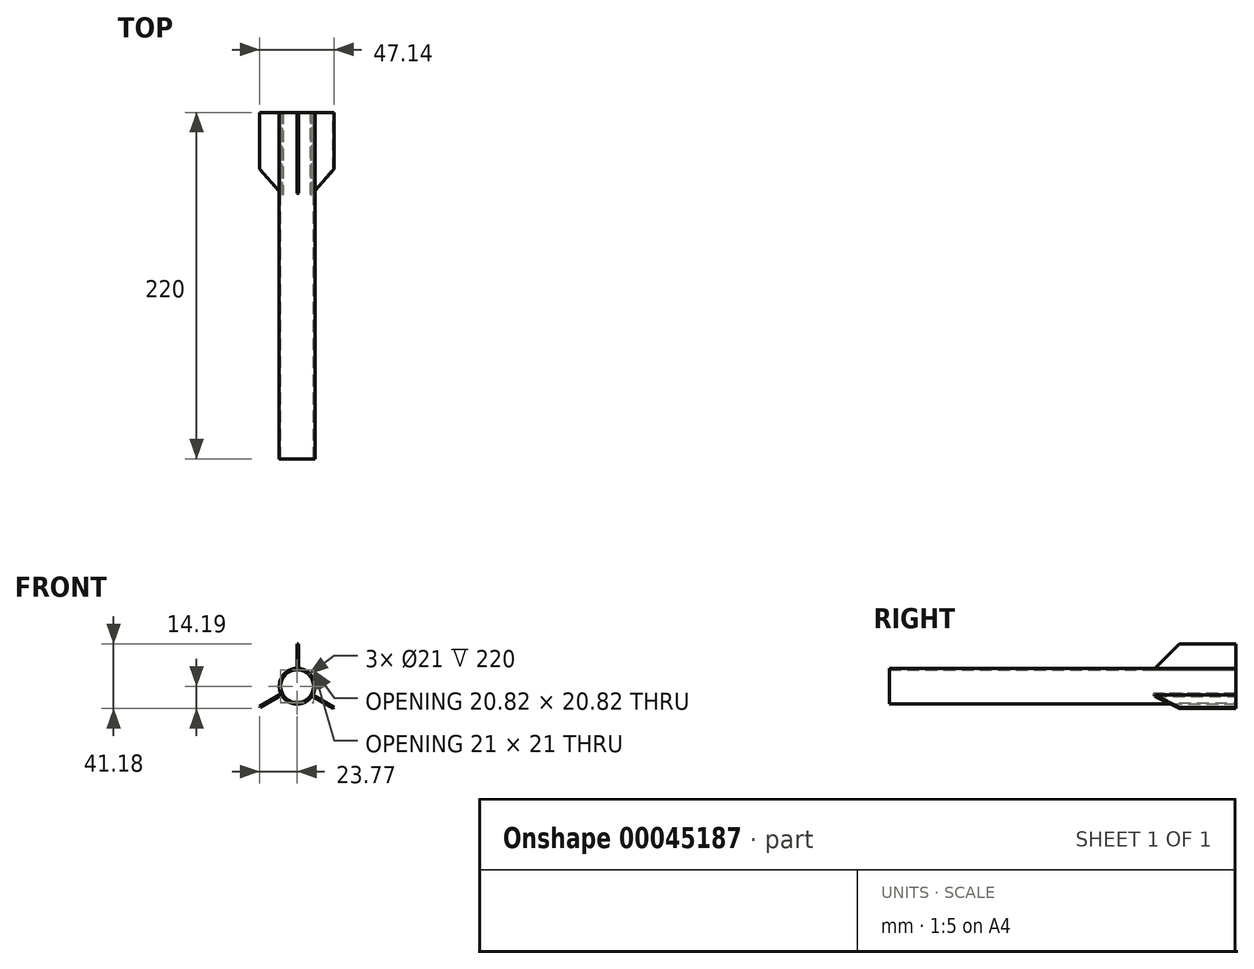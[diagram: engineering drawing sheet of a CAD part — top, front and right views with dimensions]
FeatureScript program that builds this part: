
annotation { "Feature Type Name" : "Feature", "Feature Type Description" : "" }
export const myFeature = defineFeature(function(context is Context, id is Id, definition is map)
    precondition{}
    {
        {
            var Q0;
            Q0=qCreatedBy(makeId("Front.planeOp"),FACE);
            var sketch = newSketch(context, id + "F0", { "sketchPlane" : qUnion([Q0])});
            skCircle(sketch, "E0", {"center": v(0, 0) * mm, "radius": 10.5 * mm});
            skCircle(sketch, "E1", {"center": v(0, 0) * mm, "radius": 11.3 * mm});
            skSolve(sketch);
        }
        {
            var Q0;
            Q0 = qSketchRegion(id + "F0", true);
            extrude(context, id + "F1", {"entities" : qUnion([Q0]), "depth" : 220 * mm});
        }
        {
            var Q0;
            Q0=qCreatedBy(makeId("Right.planeOp"),FACE);
            var sketch = newSketch(context, id + "F2", { "sketchPlane" : qUnion([Q0])});
            skLineSegment(sketch, "E2", {"start": v(0, 10.44) * mm, "end": v(-52.14, 10.44) * mm});
            skLineSegment(sketch, "E3", {"start": v(-52.14, 10.44) * mm, "end": v(-35.88, 26.99) * mm});
            skLineSegment(sketch, "E4", {"start": v(-35.88, 26.99) * mm, "end": v(0, 26.99) * mm});
            skLineSegment(sketch, "E5", {"start": v(0, 26.99) * mm, "end": v(0, 10.44) * mm});
            skSolve(sketch);
        }
        {
            var Q0;
            Q0=makeQuery(id+"F2.imprint","IMPRINT",FACE,{"disambiguationData":[TD([[makeQuery(id+"F2.imprint","IMPRINT",EDGE,{"derivedFrom":sQuery(id+"F2.wireOp",EDGE,"E2")}),-1.0]])]});
            extrude(context, id + "F3", {"entities" : qUnion([Q0]), "operationType" : NewBodyOperationType.ADD, "depth" : 0.8 * mm});
        }
        {
            var Q0;
            Q0=makeQuery(id+"F1.opExtrude","SWEPT_BODY",BODY,{"disambiguationData":[OSD([sQuery(id+"F0.wireOp",EDGE,"E0"),sQuery(id+"F0.wireOp",EDGE,"E1")])]});
            var Q1;
            Q1=makeQuery(id+"F1.opExtrude","SWEPT_FACE",FACE,{"disambiguationData":[OSD([sQuery(id+"F0.wireOp",EDGE,"E1")])]});
            circularPattern(context, id + "F4", {"entities" : qUnion([Q0]), "axis" : qUnion([Q1]), "angle" : 360 * degree, "instanceCount" : 3, "equalSpace" : true});
        }
    });
